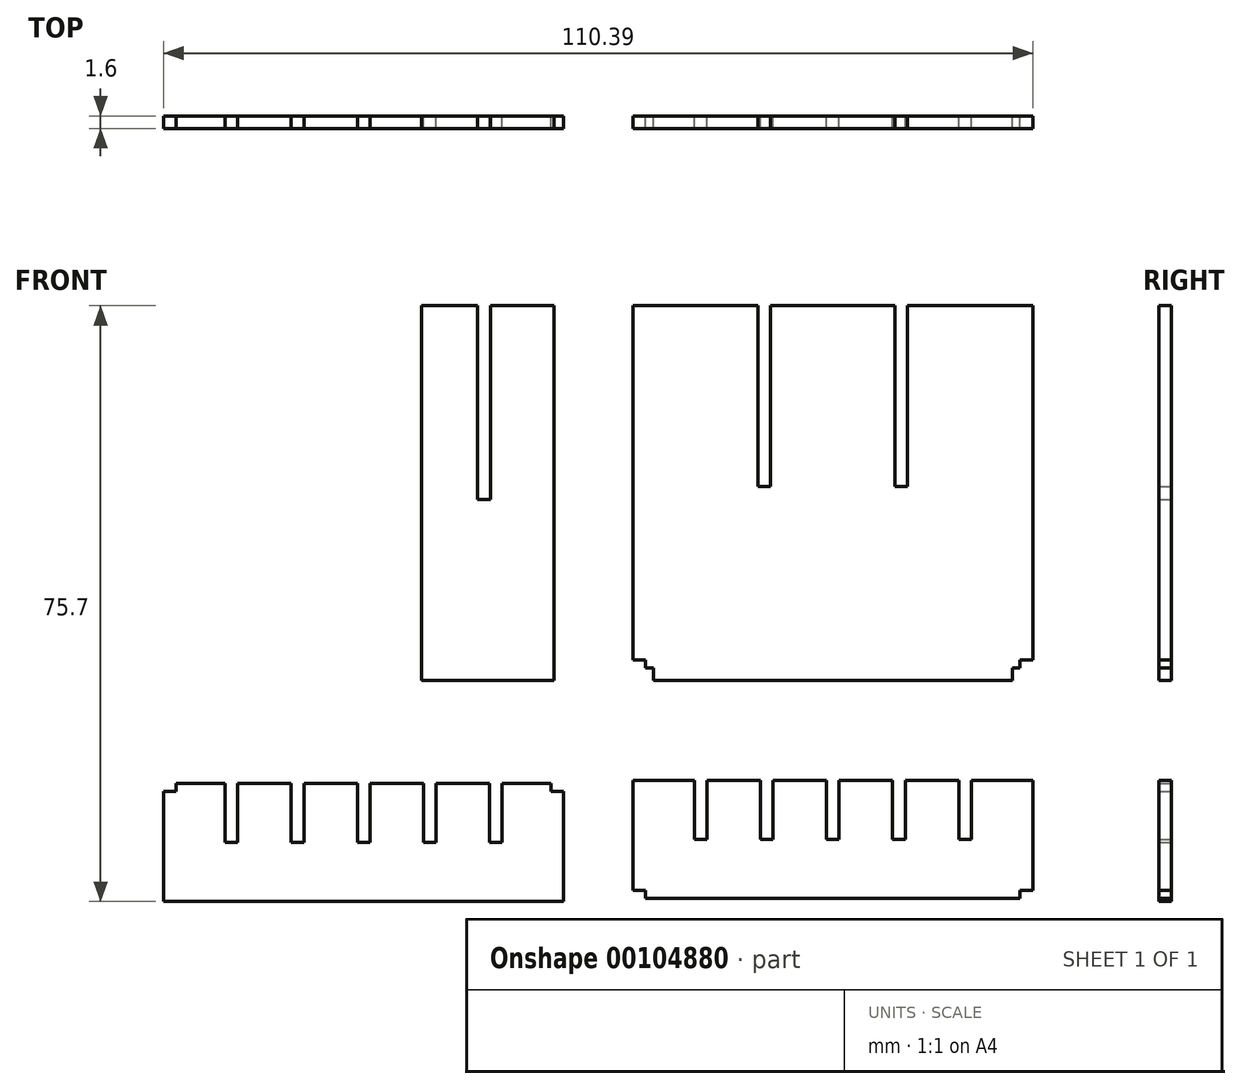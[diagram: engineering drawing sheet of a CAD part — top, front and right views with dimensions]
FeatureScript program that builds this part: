
annotation { "Feature Type Name" : "Feature", "Feature Type Description" : "" }
export const myFeature = defineFeature(function(context is Context, id is Id, definition is map)
    precondition{}
    {
        {
            var Q0;
            Q0=qCreatedBy(makeId("Front.planeOp"),FACE);
            var sketch = newSketch(context, id + "F0", { "sketchPlane" : qUnion([Q0])});
            skLineSegment(sketch, "E0.bottom", {"start": v(3.92, 15) * mm, "end": v(11.72, 15) * mm});
            skLineSegment(sketch, "E0.top", {"start": v(5.52, 0) * mm, "end": v(53.12, 0) * mm});
            skLineSegment(sketch, "E0.left", {"start": v(3.92, 15) * mm, "end": v(3.92, 1) * mm});
            skLineSegment(sketch, "E0.right", {"start": v(54.72, 15) * mm, "end": v(54.72, 1) * mm});
            skLineSegment(sketch, "E1", {"start": v(3.92, 1) * mm, "end": v(5.52, 1) * mm});
            skLineSegment(sketch, "E2", {"start": v(5.52, 1) * mm, "end": v(5.52, 0) * mm});
            skLineSegment(sketch, "E3", {"start": v(54.72, 1) * mm, "end": v(53.12, 1) * mm});
            skLineSegment(sketch, "E4", {"start": v(53.12, 1) * mm, "end": v(53.12, 0) * mm});
            skLineSegment(sketch, "E5", {"start": v(11.72, 15) * mm, "end": v(11.72, 7.5) * mm});
            skLineSegment(sketch, "E6", {"start": v(11.72, 7.5) * mm, "end": v(13.32, 7.5) * mm});
            skLineSegment(sketch, "E7", {"start": v(13.32, 7.5) * mm, "end": v(13.32, 15) * mm});
            skLineSegment(sketch, "E8.1.0.0", {"start": v(20.12, 15) * mm, "end": v(20.12, 7.5) * mm});
            skLineSegment(sketch, "E8.1.0.1", {"start": v(21.72, 7.5) * mm, "end": v(21.72, 15) * mm});
            skLineSegment(sketch, "E8.1.0.2", {"start": v(20.12, 7.5) * mm, "end": v(21.72, 7.5) * mm});
            skLineSegment(sketch, "E8.2.0.0", {"start": v(28.52, 15) * mm, "end": v(28.52, 7.5) * mm});
            skLineSegment(sketch, "E8.2.0.1", {"start": v(30.12, 7.5) * mm, "end": v(30.12, 15) * mm});
            skLineSegment(sketch, "E8.2.0.2", {"start": v(28.52, 7.5) * mm, "end": v(30.12, 7.5) * mm});
            skLineSegment(sketch, "E8.3.0.0", {"start": v(36.92, 15) * mm, "end": v(36.92, 7.5) * mm});
            skLineSegment(sketch, "E8.3.0.1", {"start": v(38.52, 7.5) * mm, "end": v(38.52, 15) * mm});
            skLineSegment(sketch, "E8.3.0.2", {"start": v(36.92, 7.5) * mm, "end": v(38.52, 7.5) * mm});
            skLineSegment(sketch, "E8.4.0.0", {"start": v(45.32, 15) * mm, "end": v(45.32, 7.5) * mm});
            skLineSegment(sketch, "E8.4.0.1", {"start": v(46.92, 7.5) * mm, "end": v(46.92, 15) * mm});
            skLineSegment(sketch, "E8.4.0.2", {"start": v(45.32, 7.5) * mm, "end": v(46.92, 7.5) * mm});
            skLineSegment(sketch, "E8.direction1", {"start": v(11.72, 7.5) * mm, "end": v(20.12, 7.5) * mm, "construction": true});
            skLineSegment(sketch, "E9.bottom", {"start": v(-54.07, 14.58) * mm, "end": v(-47.87, 14.58) * mm});
            skLineSegment(sketch, "E9.top", {"start": v(-55.67, -0.42) * mm, "end": v(-4.87, -0.42) * mm});
            skLineSegment(sketch, "E9.left", {"start": v(-55.67, 13.58) * mm, "end": v(-55.67, -0.42) * mm});
            skLineSegment(sketch, "E9.right", {"start": v(-4.87, 13.58) * mm, "end": v(-4.87, -0.42) * mm});
            skLineSegment(sketch, "E10", {"start": v(-47.87, 14.58) * mm, "end": v(-47.87, 7.08) * mm});
            skLineSegment(sketch, "E11", {"start": v(-47.87, 7.08) * mm, "end": v(-46.27, 7.08) * mm});
            skLineSegment(sketch, "E12", {"start": v(-46.27, 7.08) * mm, "end": v(-46.27, 14.58) * mm});
            skLineSegment(sketch, "E13.1.0.0", {"start": v(-39.47, 14.58) * mm, "end": v(-39.47, 7.08) * mm});
            skLineSegment(sketch, "E13.1.0.1", {"start": v(-37.87, 7.08) * mm, "end": v(-37.87, 14.58) * mm});
            skLineSegment(sketch, "E13.1.0.2", {"start": v(-39.47, 7.08) * mm, "end": v(-37.87, 7.08) * mm});
            skLineSegment(sketch, "E13.2.0.0", {"start": v(-31.07, 14.58) * mm, "end": v(-31.07, 7.08) * mm});
            skLineSegment(sketch, "E13.2.0.1", {"start": v(-29.47, 7.08) * mm, "end": v(-29.47, 14.58) * mm});
            skLineSegment(sketch, "E13.2.0.2", {"start": v(-31.07, 7.08) * mm, "end": v(-29.47, 7.08) * mm});
            skLineSegment(sketch, "E13.3.0.0", {"start": v(-22.67, 14.58) * mm, "end": v(-22.67, 7.08) * mm});
            skLineSegment(sketch, "E13.3.0.1", {"start": v(-21.07, 7.08) * mm, "end": v(-21.07, 14.58) * mm});
            skLineSegment(sketch, "E13.3.0.2", {"start": v(-22.67, 7.08) * mm, "end": v(-21.07, 7.08) * mm});
            skLineSegment(sketch, "E13.4.0.0", {"start": v(-14.27, 14.58) * mm, "end": v(-14.27, 7.08) * mm});
            skLineSegment(sketch, "E13.4.0.1", {"start": v(-12.67, 7.08) * mm, "end": v(-12.67, 14.58) * mm});
            skLineSegment(sketch, "E13.4.0.2", {"start": v(-14.27, 7.08) * mm, "end": v(-12.67, 7.08) * mm});
            skLineSegment(sketch, "E13.direction1", {"start": v(-47.87, 7.08) * mm, "end": v(-39.47, 7.08) * mm, "construction": true});
            skLineSegment(sketch, "E14", {"start": v(-55.67, 13.58) * mm, "end": v(-54.07, 13.58) * mm});
            skLineSegment(sketch, "E15", {"start": v(-54.07, 13.58) * mm, "end": v(-54.07, 14.58) * mm});
            skLineSegment(sketch, "E16", {"start": v(-6.47, 14.58) * mm, "end": v(-6.47, 13.58) * mm});
            skLineSegment(sketch, "E17", {"start": v(-6.47, 13.58) * mm, "end": v(-4.87, 13.58) * mm});
            skLineSegment(sketch, "E18.trimOffspring", {"start": v(-46.27, 14.58) * mm, "end": v(-39.47, 14.58) * mm});
            skLineSegment(sketch, "E19.trimOffspring", {"start": v(-37.87, 14.58) * mm, "end": v(-31.07, 14.58) * mm});
            skLineSegment(sketch, "E20.trimOffspring", {"start": v(-29.47, 14.58) * mm, "end": v(-22.67, 14.58) * mm});
            skLineSegment(sketch, "E21.trimOffspring", {"start": v(-21.07, 14.58) * mm, "end": v(-14.27, 14.58) * mm});
            skLineSegment(sketch, "E22.trimOffspring", {"start": v(-12.67, 14.58) * mm, "end": v(-6.47, 14.58) * mm});
            skLineSegment(sketch, "E23.trimOffspring", {"start": v(13.32, 15) * mm, "end": v(20.12, 15) * mm});
            skLineSegment(sketch, "E24.trimOffspring", {"start": v(21.72, 15) * mm, "end": v(28.52, 15) * mm});
            skLineSegment(sketch, "E25.trimOffspring", {"start": v(30.12, 15) * mm, "end": v(36.92, 15) * mm});
            skLineSegment(sketch, "E26.trimOffspring", {"start": v(38.52, 15) * mm, "end": v(45.32, 15) * mm});
            skLineSegment(sketch, "E27.trimOffspring", {"start": v(46.92, 15) * mm, "end": v(54.72, 15) * mm});
            skPoint(sketch, "E28.orphan", {"position": v(54.72, 0) * mm});
            skLineSegment(sketch, "E29.top", {"start": v(3.92, 75.28) * mm, "end": v(19.82, 75.28) * mm});
            skPoint(sketch, "E30.orphan", {"position": v(3.92, 27.68) * mm});
            skLineSegment(sketch, "E31", {"start": v(19.82, 75.28) * mm, "end": v(19.82, 52.28) * mm});
            skLineSegment(sketch, "E32", {"start": v(19.82, 52.28) * mm, "end": v(21.42, 52.28) * mm});
            skLineSegment(sketch, "E33", {"start": v(21.42, 52.28) * mm, "end": v(21.42, 75.28) * mm});
            skLineSegment(sketch, "E34.1.0.0", {"start": v(37.22, 75.28) * mm, "end": v(37.22, 52.28) * mm});
            skLineSegment(sketch, "E34.1.0.1", {"start": v(38.82, 52.28) * mm, "end": v(38.82, 75.28) * mm});
            skLineSegment(sketch, "E34.1.0.2", {"start": v(37.22, 52.28) * mm, "end": v(38.82, 52.28) * mm});
            skLineSegment(sketch, "E35.trimOffspring", {"start": v(21.42, 75.28) * mm, "end": v(37.22, 75.28) * mm});
            skLineSegment(sketch, "E36", {"start": v(38.82, 75.28) * mm, "end": v(54.72, 75.28) * mm});
            skLineSegment(sketch, "E37", {"start": v(-6.08, 27.68) * mm, "end": v(-6.08, 75.28) * mm});
            skLineSegment(sketch, "E38", {"start": v(-6.08, 75.28) * mm, "end": v(-14.18, 75.28) * mm});
            skLineSegment(sketch, "E39", {"start": v(-14.18, 75.28) * mm, "end": v(-14.18, 50.68) * mm});
            skLineSegment(sketch, "E40", {"start": v(-14.18, 50.68) * mm, "end": v(-15.78, 50.68) * mm});
            skLineSegment(sketch, "E41", {"start": v(-15.78, 50.68) * mm, "end": v(-15.78, 75.28) * mm});
            skLineSegment(sketch, "E42", {"start": v(-15.78, 75.28) * mm, "end": v(-22.88, 75.28) * mm});
            skLineSegment(sketch, "E43", {"start": v(-22.88, 75.28) * mm, "end": v(-22.88, 27.68) * mm});
            skLineSegment(sketch, "E44", {"start": v(-22.88, 27.68) * mm, "end": v(-6.08, 27.68) * mm});
            skLineSegment(sketch, "E45", {"start": v(3.92, 75.28) * mm, "end": v(3.92, 30.28) * mm});
            skLineSegment(sketch, "E46", {"start": v(54.72, 75.28) * mm, "end": v(54.72, 30.28) * mm});
            skLineSegment(sketch, "E47", {"start": v(52.12, 27.68) * mm, "end": v(6.52, 27.68) * mm});
            skLineSegment(sketch, "E48", {"start": v(6.52, 27.68) * mm, "end": v(6.52, 29.28) * mm});
            skLineSegment(sketch, "E49", {"start": v(6.52, 29.28) * mm, "end": v(5.52, 29.28) * mm});
            skLineSegment(sketch, "E50", {"start": v(5.52, 29.28) * mm, "end": v(5.52, 30.28) * mm});
            skLineSegment(sketch, "E51", {"start": v(5.52, 30.28) * mm, "end": v(3.92, 30.28) * mm});
            skLineSegment(sketch, "E52", {"start": v(52.12, 27.68) * mm, "end": v(52.12, 29.28) * mm});
            skLineSegment(sketch, "E53", {"start": v(52.12, 29.28) * mm, "end": v(53.12, 29.28) * mm});
            skLineSegment(sketch, "E54", {"start": v(53.12, 29.28) * mm, "end": v(53.12, 30.28) * mm});
            skLineSegment(sketch, "E55", {"start": v(53.12, 30.28) * mm, "end": v(54.72, 30.28) * mm});
            skPoint(sketch, "E56.orphan", {"position": v(54.72, 27.68) * mm});
            skSolve(sketch);
        }
        {
            var Q0;
            Q0=makeQuery(id+"F0.imprint","IMPRINT",FACE,{"disambiguationData":[TD([[makeQuery(id+"F0.imprint","IMPRINT",EDGE,{"derivedFrom":sQuery(id+"F0.wireOp",EDGE,"E37")}),1.0]])]});
            var Q1;
            Q1=makeQuery(id+"F0.imprint","IMPRINT",FACE,{"disambiguationData":[TD([[makeQuery(id+"F0.imprint","IMPRINT",EDGE,{"derivedFrom":sQuery(id+"F0.wireOp",EDGE,"E0.bottom")}),-1.0]])]});
            var Q2;
            Q2=makeQuery(id+"F0.imprint","IMPRINT",FACE,{"disambiguationData":[TD([[makeQuery(id+"F0.imprint","IMPRINT",EDGE,{"derivedFrom":sQuery(id+"F0.wireOp",EDGE,"E9.bottom")}),-1.0]])]});
            var Q3;
            Q3=makeQuery(id+"F0.imprint","IMPRINT",FACE,{"disambiguationData":[TD([[makeQuery(id+"F0.imprint","IMPRINT",EDGE,{"derivedFrom":sQuery(id+"F0.wireOp",EDGE,"E29.top")}),-1.0]])]});
            extrude(context, id + "F1", {"entities" : qUnion([Q0, Q1, Q2, Q3]), "depth" : 1.6 * mm});
        }
    });
